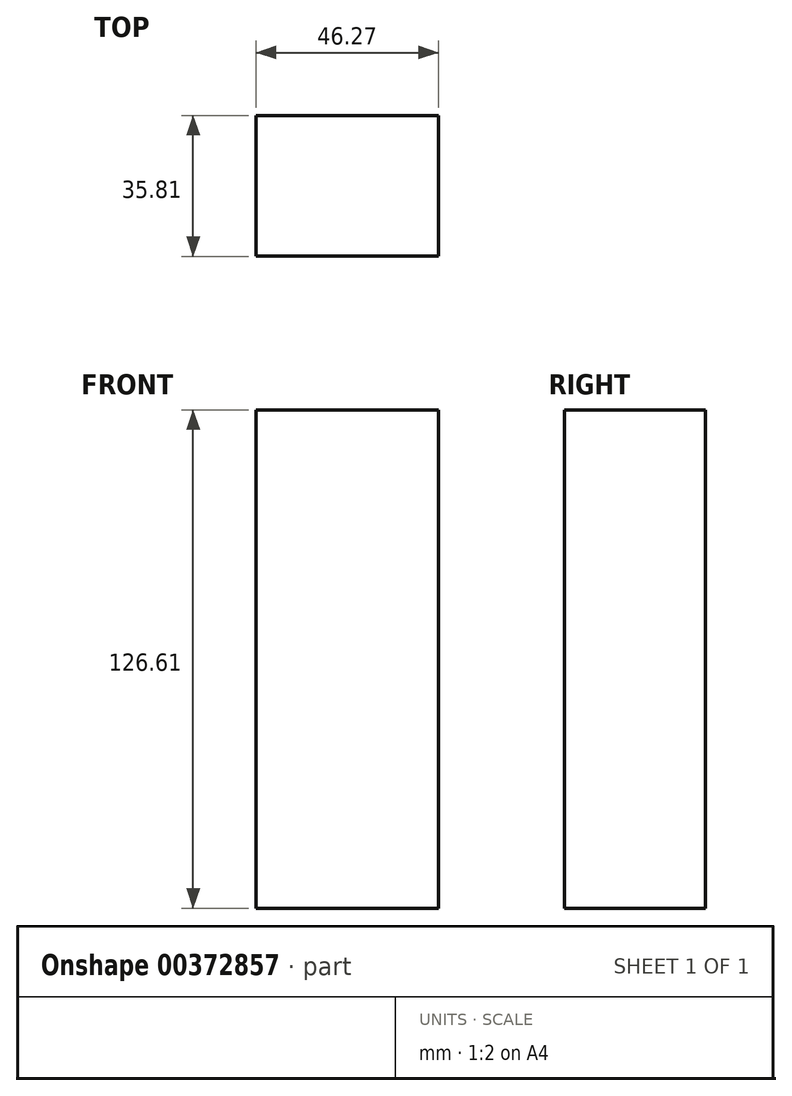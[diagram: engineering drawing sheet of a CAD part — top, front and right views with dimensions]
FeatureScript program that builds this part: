
annotation { "Feature Type Name" : "Feature", "Feature Type Description" : "" }
export const myFeature = defineFeature(function(context is Context, id is Id, definition is map)
    precondition{}
    {
        {
            var Q0;
            Q0=qCreatedBy(makeId("Top.planeOp"),FACE);
            var sketch = newSketch(context, id + "F0", { "sketchPlane" : qUnion([Q0])});
            skLineSegment(sketch, "E0.bottom", {"start": v(0, 0) * mm, "end": v(46.27, 0) * mm});
            skLineSegment(sketch, "E0.top", {"start": v(0, -35.8) * mm, "end": v(46.27, -35.8) * mm});
            skLineSegment(sketch, "E0.left", {"start": v(0, 0) * mm, "end": v(0, -35.8) * mm});
            skLineSegment(sketch, "E0.right", {"start": v(46.27, 0) * mm, "end": v(46.27, -35.8) * mm});
            skSolve(sketch);
        }
        {
            var Q0;
            Q0 = qSketchRegion(id + "F0", true);
            extrude(context, id + "F1", {"entities" : qUnion([Q0]), "depth" : 126.6 * mm});
        }
    });
